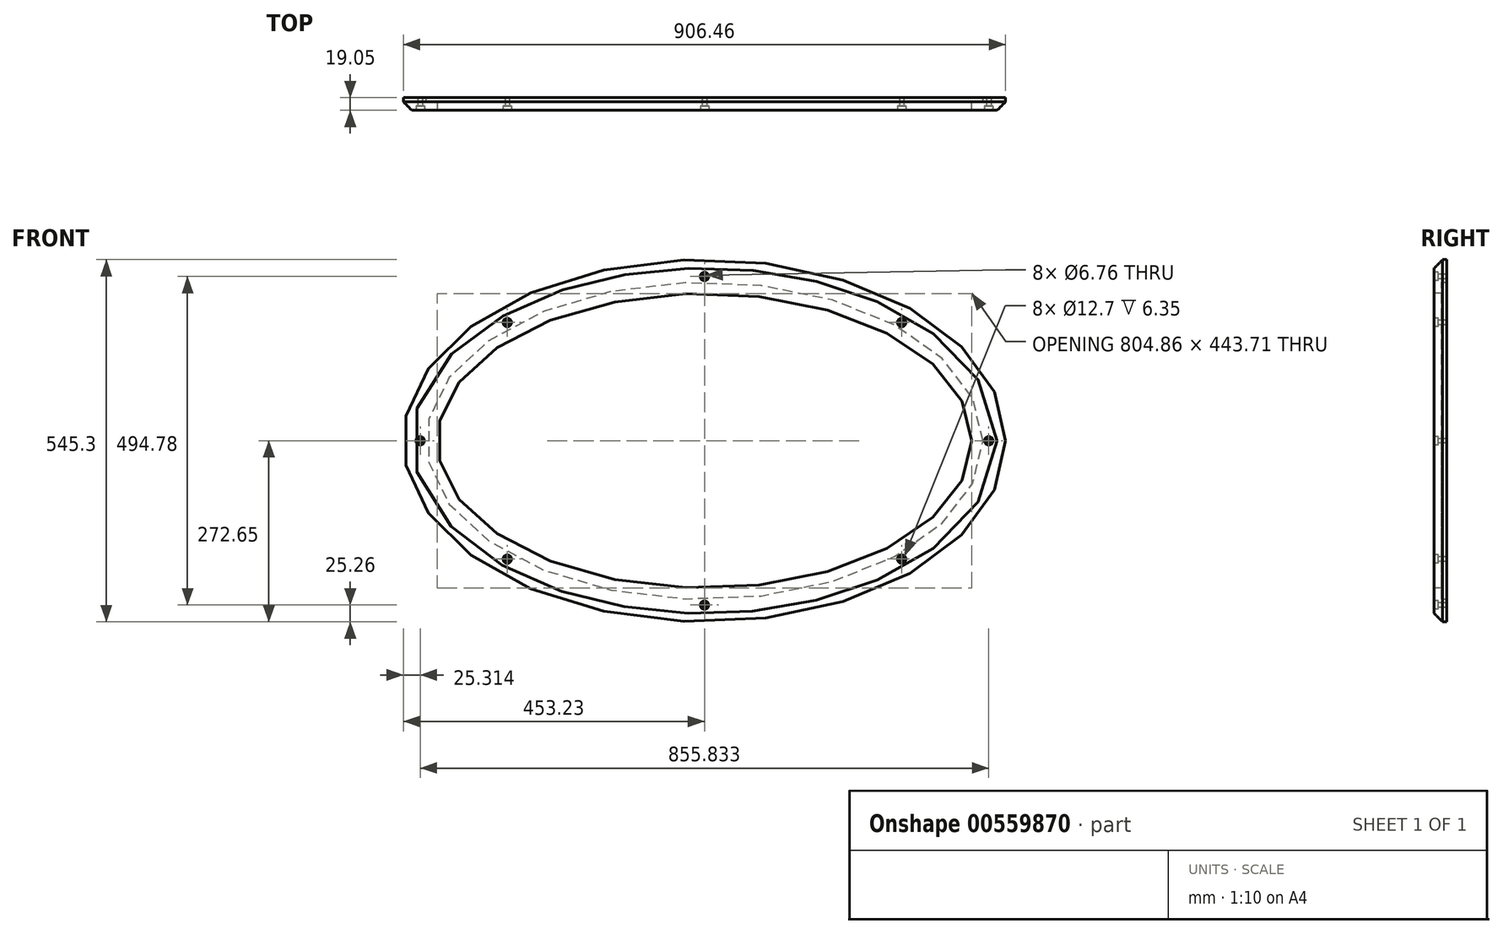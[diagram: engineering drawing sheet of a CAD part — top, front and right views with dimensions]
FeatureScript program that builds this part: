
annotation { "Feature Type Name" : "Feature", "Feature Type Description" : "" }
export const myFeature = defineFeature(function(context is Context, id is Id, definition is map)
    precondition{}
    {
        {
            var Q0;
            Q0=qCreatedBy(makeId("Front.planeOp"),FACE);
            var sketch = newSketch(context, id + "F0", { "sketchPlane" : qUnion([Q0])});
            skEllipse(sketch, "E0", {"center": v(0, 0) * mm, "majorRadius": 453.23 * mm, "minorRadius": 272.65 * mm, "majorAxis": v(1, 0)});
            skSolve(sketch);
        }
        {
            var Q0;
            Q0=makeQuery(id+"F0.imprint","IMPRINT",FACE,{"disambiguationData":[TD([[makeQuery(id+"F0.imprint","IMPRINT",EDGE,{"derivedFrom":sQuery(id+"F0.wireOp",EDGE,"E0")}),1.0]])]});
            var sketch = newSketch(context, id + "F1", { "sketchPlane" : qUnion([Q0])});
            skEllipse(sketch, "E1", {"center": v(0, 0) * mm, "majorRadius": 402.43 * mm, "minorRadius": 221.85 * mm, "majorAxis": v(1, 0)});
            skSolve(sketch);
        }
        {
            var Q0;
            Q0=makeQuery(id+"F0.imprint","IMPRINT",FACE,{"disambiguationData":[TD([[makeQuery(id+"F0.imprint","IMPRINT",EDGE,{"derivedFrom":sQuery(id+"F0.wireOp",EDGE,"E0")}),1.0]])]});
            extrude(context, id + "F2", {"entities" : qUnion([Q0]), "depth" : 19.05 * mm, "offsetDistance" : 25.4 * mm});
        }
        {
            var Q0;
            Q0 = qSketchRegion(id + "F1", true);
            var Q1;
            Q1=sQuery(id+"F1.wireOp",EDGE,"E1");
            extrude(context, id + "F3", {"entities" : qUnion([Q0]), "operationType" : NewBodyOperationType.REMOVE, "surfaceEntities" : qUnion([Q1]), "depth" : 19.05 * mm, "offsetDistance" : 25.4 * mm});
        }
        {
            var Q0;
            Q0=makeQuery(id+"F3.boolean.opBoolean","COPY",EDGE,{"derivedFrom":makeQuery(id+"F3.opExtrude","CAP_EDGE",EDGE,{"disambiguationData":[OSD([sQuery(id+"F1.wireOp",EDGE,"E1")])],"isStart":false})});
            var Q1;
            Q1=makeQuery(id+"F2.opExtrude","CAP_EDGE",EDGE,{"disambiguationData":[OSD([sQuery(id+"F0.wireOp",EDGE,"E0")])],"isStart":false});
            chamfer(context, id + "F4", {"entities" : qUnion([Q0, Q1]), "width" : 12.7 * mm, "tangentPropagation" : true});
        }
        {
            var Q0;
            Q0=makeQuery(id+"F2.opExtrude","CAP_FACE",FACE,{"disambiguationData":[OSD([sQuery(id+"F0.wireOp",EDGE,"E0")])],"isStart":false});
            var sketch = newSketch(context, id + "F5", { "sketchPlane" : qUnion([Q0])});
            skPoint(sketch, "E2", {"position": v(0, 247.4) * mm});
            skPoint(sketch, "E3", {"position": v(-427.92, 0) * mm});
            skPoint(sketch, "E4", {"position": v(-296.82, 178.08) * mm});
            skPoint(sketch, "E5", {"position": v(-296.82, -178.13) * mm});
            skPoint(sketch, "E6.MirrorP", {"position": v(296.82, -178.13) * mm});
            skPoint(sketch, "E7.MirrorP", {"position": v(296.82, 178.08) * mm});
            skPoint(sketch, "E8.MirrorP", {"position": v(427.92, 0) * mm});
            skPoint(sketch, "E9.MirrorP", {"position": v(0, -247.4) * mm});
            skSolve(sketch);
        }
        {
            var Q0;
            Q0=sQuery(id+"F5.wireOp",VERTEX,"E3");
            var Q1;
            Q1=sQuery(id+"F5.wireOp",VERTEX,"E4");
            var Q2;
            Q2=sQuery(id+"F5.wireOp",VERTEX,"E2");
            var Q3;
            Q3=sQuery(id+"F5.wireOp",VERTEX,"E7.MirrorP");
            var Q4;
            Q4=sQuery(id+"F5.wireOp",VERTEX,"E8.MirrorP");
            var Q5;
            Q5=sQuery(id+"F5.wireOp",VERTEX,"E6.MirrorP");
            var Q6;
            Q6=sQuery(id+"F5.wireOp",VERTEX,"E9.MirrorP");
            var Q7;
            Q7=sQuery(id+"F5.wireOp",VERTEX,"E5");
            var Q8;
            Q8=makeQuery(id+"F2.opExtrude","SWEPT_BODY",BODY,{"disambiguationData":[OSD([sQuery(id+"F0.wireOp",EDGE,"E0")])]});
            hole(context, id + "F6", {"style" : HoleStyle.C_BORE, "endStyle" : HoleEndStyle.THROUGH, "holeDiameter" : 6.76 * mm, "cBoreDiameter" : 12.7 * mm, "cBoreDepth" : 6.35 * mm, "isTappedThrough" : true, "tappedDepth" : 12.7 * mm, "tapClearance" : 3, "startFromSketch" : true, "locations" : qUnion([Q0, Q1, Q2, Q3, Q4, Q5, Q6, Q7]), "scope" : qUnion([Q8])});
        }
        {
            var Q0;
            Q0=makeQuery(id+"F1.imprint","IMPRINT",FACE,{"disambiguationData":[TD([[makeQuery(id+"F1.imprint","IMPRINT",EDGE,{"derivedFrom":sQuery(id+"F1.wireOp",EDGE,"E1")}),-1.0]])]});
            var sketch = newSketch(context, id + "F7", { "sketchPlane" : qUnion([Q0])});
            skEllipse(sketch, "E10", {"center": v(0, 0) * mm, "majorRadius": 419.1 * mm, "minorRadius": 238.52 * mm, "majorAxis": v(1, 0)});
            skSolve(sketch);
        }
        {
            var Q0;
            Q0=makeQuery(id+"F7.imprint","IMPRINT",FACE,{"disambiguationData":[TD([[makeQuery(id+"F7.imprint","IMPRINT",EDGE,{"derivedFrom":sQuery(id+"F7.wireOp",EDGE,"E10")}),1.0]])]});
            var Q1;
            Q1=sQuery(id+"F1.wireOp",EDGE,"E1");
            var Q2;
            Q2=sQuery(id+"F7.wireOp",EDGE,"E10");
            extrude(context, id + "F8", {"entities" : qUnion([Q0]), "operationType" : NewBodyOperationType.REMOVE, "surfaceEntities" : qUnion([Q1, Q2]), "depth" : 7.62 * mm, "hasOffset" : true, "offsetDistance" : 7.62 * mm});
        }
    });
